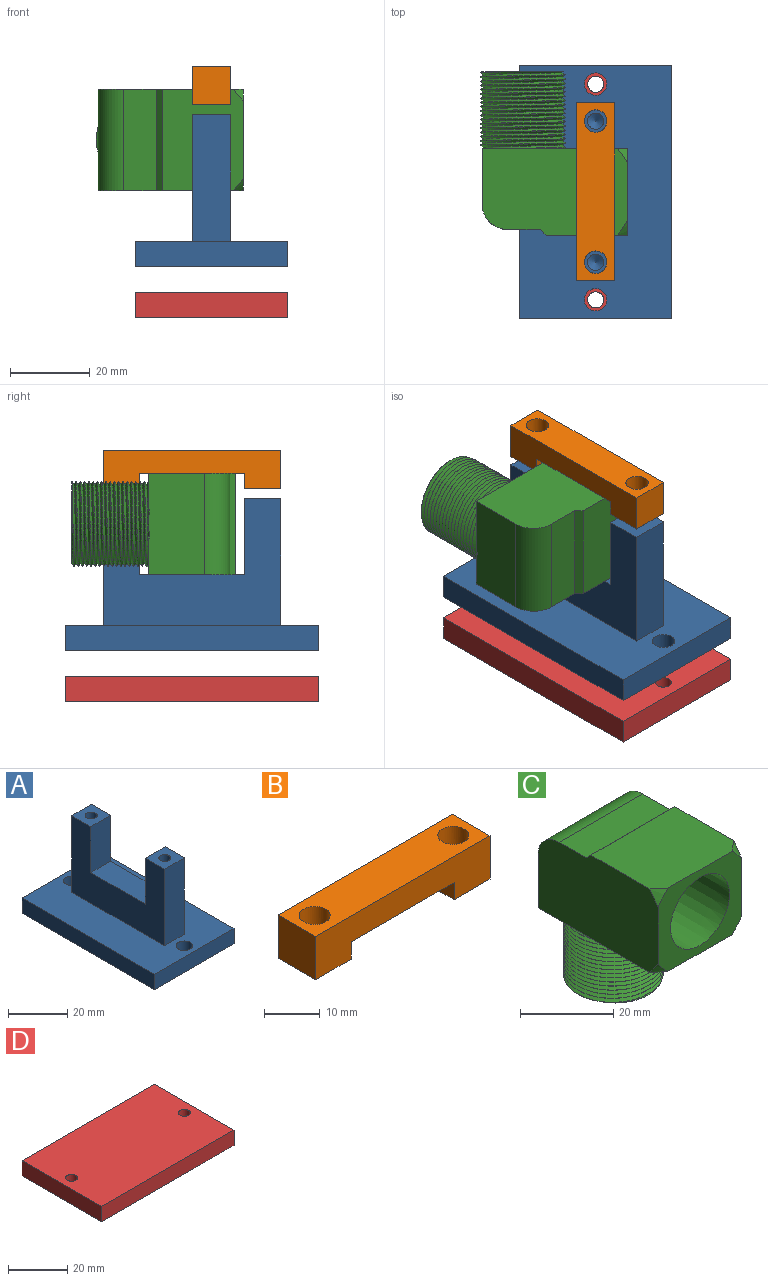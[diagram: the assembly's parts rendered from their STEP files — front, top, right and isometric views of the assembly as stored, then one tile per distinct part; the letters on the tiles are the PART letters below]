
ASSEMBLY  parts=4 mates=3
PART A: 21 faces, bbox 38.1x63.5x38.1 mm
  f0: plane 9.53x9.14mm, normal (0,0,1), area 74.3mm2, adj f1,f7,f9,f14,f18
  f1: plane 44.45x31.75mm, normal (1,0,0), area 912.9mm2, adj f0,f8,f9,f10,f11,f12,f13,f14
  f2: plane 38.1x6.35mm, normal (0,1,0), area 241.9mm2, adj f3,f5,f6,f10
  f3: plane 63.5x6.35mm, normal (-1,0,0), area 403.2mm2, adj f2,f4,f6,f10
  f4: plane 38.1x6.35mm, normal (0,-1,0), area 241.9mm2, adj f3,f5,f6,f10
  f5: plane 63.5x6.35mm, normal (1,0,0), area 403.2mm2, adj f2,f4,f6,f10
  f6: plane 63.5x38.1mm, normal (0,0,-1), area 2369.9mm2, adj f2,f3,f4,f5,f19,f20
  f7: plane 44.45x31.75mm, normal (-1,0,0), area 912.9mm2, adj f0,f8,f9,f10,f11,f12,f13,f14
  f8: plane 31.75x9.53mm, normal (0,1,0), area 302.4mm2, adj f1,f7,f10,f11
  f9: plane 31.75x9.53mm, normal (0,-1,0), area 302.4mm2, adj f0,f1,f7,f10
  f10: plane 63.5x38.1mm, normal (0,0,1), area 1946.5mm2, adj f1,f2,f3,f4,f5,f7,f8,f9
  f11: plane 9.53x9.14mm, normal (0,0,1), area 74.3mm2, adj f1,f7,f8,f12,f16
  f12: plane 19.05x9.53mm, normal (0,-1,0), area 181.5mm2, adj f1,f7,f11,f13
  f13: plane 26.16x9.53mm, normal (0,0,1), area 249.2mm2, adj f1,f7,f12,f14
  f14: plane 19.05x9.53mm, normal (0,1,0), area 181.5mm2, adj f0,f1,f7,f13
  f15: cone r=0mm half-angle=59deg, axis (0,0,1), area 14.9mm2, adj f16
  f16: cylinder r=2.02mm len=15.08mm, axis (0,0,1), area 191.3mm2, adj f11,f15
  f17: cone r=0mm half-angle=59deg, axis (0,0,1), area 14.9mm2, adj f18
  f18: cylinder r=2.02mm len=15.08mm, axis (0,0,1), area 191.3mm2, adj f0,f17
  f19: cylinder r=2.81mm len=6.35mm, axis (0,0,1), area 112mm2, adj f6,f10
  f20: cylinder r=2.81mm len=6.35mm, axis (0,0,1), area 112mm2, adj f6,f10
PART B: 12 faces, bbox 44.5x9.5x9.5 mm
  f0: plane 9.53x9.14mm, normal (0,0,-1), area 62.3mm2, adj f1,f2,f3,f7,f11
  f1: plane 44.45x9.53mm, normal (0,1,0), area 323.7mm2, adj f0,f2,f4,f5,f6,f7,f8,f9
  f2: plane 9.53x9.53mm, normal (-1,0,0), area 90.7mm2, adj f0,f1,f3,f5
  f3: plane 44.45x9.53mm, normal (0,-1,0), area 323.7mm2, adj f0,f2,f4,f5,f6,f7,f8,f9
  f4: plane 9.53x9.53mm, normal (1,0,0), area 90.7mm2, adj f1,f3,f5,f6
  f5: plane 44.45x9.53mm, normal (0,0,1), area 373.9mm2, adj f1,f2,f3,f4,f10,f11
  f6: plane 9.53x9.14mm, normal (0,0,-1), area 62.3mm2, adj f1,f3,f4,f8,f10
  f7: plane 9.53x3.81mm, normal (1,0,0), area 36.3mm2, adj f0,f1,f3,f9
  f8: plane 9.53x3.81mm, normal (-1,0,0), area 36.3mm2, adj f1,f3,f6,f9
  f9: plane 26.16x9.53mm, normal (0,0,-1), area 249.2mm2, adj f1,f3,f7,f8
  f10: cylinder r=2.81mm len=9.53mm, axis (0,0,-1), area 168mm2, adj f5,f6
  f11: cylinder r=2.81mm len=9.53mm, axis (0,0,-1), area 168mm2, adj f0,f5
PART C: 24 faces, bbox 29.8x37.6x43.8 mm
  f0: cylinder r=7.11mm len=27.94mm, axis (0,0,-1), area 1118.8mm2, adj f1,f9,f10,f16
  f1: cone r=8.9mm half-angle=1deg, axis (0,-1,0), area 1530.6mm2, adj f0,f5,f10
  f2: cylinder r=10.67mm len=21.34mm, axis (0,0,1), area 51.4mm2, adj f3,f9,f11,f14,f15
  f3: plane 36.55x25.63mm, normal (0,0,-1), area 559.8mm2, adj f2,f4,f5,f6,f8,f12,f13,f22
  f4: plane 36.67x22.2mm, normal (-1,0,0), area 753.3mm2, adj f3,f5,f7,f8,f17,f18,f19,f21
  f5: plane 25.4x21.84mm, normal (0,-1,0), area 286.3mm2, adj f1,f3,f4,f6,f7,f20,f21,f22
  f6: plane 36.67x22.2mm, normal (1,0,0), area 753.3mm2, adj f3,f5,f7,f8,f17,f18,f19,f20
  f7: plane 25.63x20.55mm, normal (0,0,1), area 508.7mm2, adj f4,f5,f6,f17,f20,f21
  f8: plane 25.4x14.02mm, normal (0,1,0), area 355.4mm2, adj f3,f4,f6,f11,f12,f13,f19
  f9: plane 21.24x21.22mm, normal (0,0,-1), area 170.6mm2, adj f0,f2,f11,f15
  f10: plane 16.74x14.55mm, normal (0,-1,0), area 157.1mm2, adj f0,f1,f16
  f11: bspline ~21.33x21.31mm, area 1202.7mm2, adj f2,f8,f9,f12,f13,f14,f15
  f12: cylinder r=10.67mm len=10.16mm, axis (0,0,-1), area 6.3mm2, adj f3,f8,f11,f14
  f13: cylinder r=10.67mm len=12.62mm, axis (0,0,-1), area 2mm2, adj f3,f8,f11
  f14: plane 1.03x0.89mm, normal (0,1,0), area 0.5mm2, adj f2,f11,f12,f15
  f15: bspline ~21.34x21.34mm, area 1173.5mm2, adj f2,f9,f11,f14
  f16: plane 11.3x2.79mm, normal (0,0,-1), area 22mm2, adj f0,f10
  f17: plane 25.4x1.47mm, normal (0,0.71,0.71), area 52.9mm2, adj f4,f6,f7,f18
  f18: plane 25.4x8.18mm, normal (0,0,1), area 207.7mm2, adj f4,f6,f17,f19
  f19: cylinder r=6.35mm len=25.4mm, axis (1,0,0), area 253.4mm2, adj f4,f6,f8,f18
  f20: cone r=14.62mm half-angle=40deg, axis (0,1,0), area 8.3mm2, adj f5,f6,f7
  f21: cone r=14.62mm half-angle=40deg, axis (0,1,0), area 8.3mm2, adj f4,f5,f7
  f22: cone r=14.62mm half-angle=40deg, axis (0,1,0), area 8.3mm2, adj f3,f5,f6
  f23: cone r=14.62mm half-angle=40deg, axis (0,1,0), area 8.3mm2, adj f3,f4,f5
PART D: 8 faces, bbox 63.5x38.1x6.4 mm
  f0: plane 63.5x6.35mm, normal (0,1,0), area 403.2mm2, adj f1,f3,f4,f5
  f1: plane 38.1x6.35mm, normal (-1,0,0), area 241.9mm2, adj f0,f2,f4,f5
  f2: plane 63.5x6.35mm, normal (0,-1,0), area 403.2mm2, adj f1,f3,f4,f5
  f3: plane 38.1x6.35mm, normal (1,0,0), area 241.9mm2, adj f0,f2,f4,f5
  f4: plane 63.5x38.1mm, normal (0,0,1), area 2393.7mm2, adj f0,f1,f2,f3,f6,f7
  f5: plane 63.5x38.1mm, normal (0,0,-1), area 2393.7mm2, adj f0,f1,f2,f3,f6,f7
  f6: cylinder r=2.02mm len=6.35mm, axis (0,0,-1), area 80.6mm2, adj f4,f5
  f7: cylinder r=2.02mm len=6.35mm, axis (0,0,-1), area 80.6mm2, adj f4,f5
PLACE A t=(-3.31,3.78,-8.7)mm
PLACE B rot(axis=(0,0,-1),90deg) t=(-3.31,3.78,31.94)mm
PLACE C rot(axis=(0.58,-0.58,0.58),120deg) t=(4.62,14.71,21.22)mm
PLACE D rot(axis=(0,0,1),90deg) t=(-3.31,3.78,-21.4)mm
MATE fastened D.f7 <-> A.f19  axis (0,0,1) through (-3.31,-23.2,-15.05)mm
MATE fastened C.f4 <-> A.f13  axis (0,0,-1) through (4.62,3.78,10.35)mm
MATE fastened B.f9 <-> C.f6  axis (0,0,-1) through (1.45,3.78,35.75)mm
